# Revit family: Plum Fix_Toilet_Argent_Alto Plus PWD BTW
name_source: partatom
category: Plumbing Fixtures
revit_build: Autodesk Revit 2016 (Build: 20150220_1215(x64)
units: mm (PartAtom-declared; Revit-internal decimal feet)

## family parameters
Always vertical = Yes
Cut with Voids When Loaded = Yes
OmniClass Number = 23.45.05.21.11
OmniClass Title = Water Closets
Part Type = Normal
Room Calculation Point = No
Round Connector Dimension = Use Diameter
Shared = No
Work Plane-Based = No

## types (4) — shared parameters
Back Rest Height = 700 mm  [stored 2.29659 ft]
Back Rest Material = z_Argent_Rubber
Back Rest Support Material = z_Argent_Stainless Steel
Back rest = 700 mm  [stored 2.29659 ft]
Body Material = z_Argent_Ceramic White
CW Connection = Yes
Description = Alto Plus PWD Back-To-Wall Toilet Suite with Single Flap Seat, S&P Traps
Flush Material = z_Argent_Stainless Steel
HW Connection = No
Manufacturer = Argent
Manufacturer_Overall Depth = 800 mm  [stored 2.62467 ft]
Manufacturer_Overall Height = 870 mm  [stored 2.85433 ft]
Manufacturer_Overall Width = 385 mm  [stored 1.26312 ft]
Manufacturer_URL__Product Specific = https://www.argentaust.com.au
ModifiedIssue_ANZRS = 20190503 $
Trap Offset = 170 mm  [stored 0.557743 ft]
Trap Offset Value = 170 mm  [stored 0.557743 ft]
URL = https://www.argentaust.com.au
Vent Connection = No
Waste Connection = Yes
zero-valued in all types: CWFU, Cost, HWFU, WFU

## per-type parameters (varying)
| type | Angle Offset | Back Rest Visibility | Bottom Entry | Manufacturer_Spec Code | Model | Rear Entry | Trap Angle | Without Back Rest |
| Rear Water Entry | 95 mm | No | No | 805701T4RDB | 805701T4RDB | Yes | -90.00° | Yes |
| Bottom Water Entry | 0 mm  [stored 0 ft] | No | Yes | 805701T4BDB | 805701T4BDB | No | 0.00° | Yes |
| Bottom Water Entry with Backrest | 0 mm  [stored 0 ft] | Yes | Yes | 805701T4BPB | 805701T4BPB | No | 0.00° | No |
| Rear Water Entry with Backrest | 95 mm | Yes | No | 805701T4RPB | 805701T4RPB | Yes | -90.00° | No |

note: column(s) folded — value = type name in every type: Type Comments

note: [stored X ft] marks values corroborated as IEEE doubles in the binary element streams (Revit-internal decimal feet)

## geometry (parser evidence)
native form markers: Sweep x5
no freeform markers — native parametric forms only
